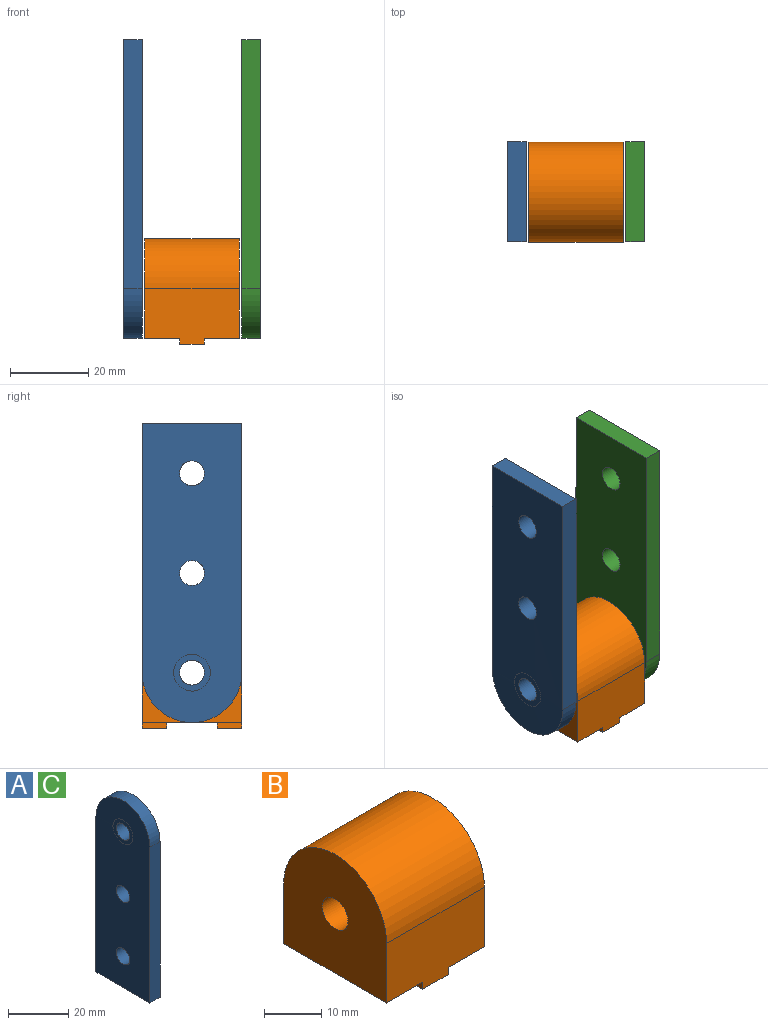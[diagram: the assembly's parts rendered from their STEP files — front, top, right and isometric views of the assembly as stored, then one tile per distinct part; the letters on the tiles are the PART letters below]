
ASSEMBLY  parts=3 mates=3
PART A: 11 faces, bbox 4.8x25.4x76.2 mm
  f0: cylinder r=12.7mm len=25.4mm, axis (-1,0,0), area 190mm2, adj f1,f5,f6,f7
  f1: plane 63.5x4.76mm, normal (0,-1,0), area 302.4mm2, adj f0,f2,f6,f7
  f2: plane 25.4x4.76mm, normal (0,0,-1), area 121mm2, adj f1,f5,f6,f7
  f3: cylinder r=3.17mm len=6.35mm, axis (-1,0,0), area 95mm2, adj f6,f7
  f4: cylinder r=3.17mm len=6.35mm, axis (-1,0,0), area 95mm2, adj f6,f7
  f5: plane 63.5x4.76mm, normal (0,1,0), area 302.4mm2, adj f0,f2,f6,f7
  f6: plane 76.21x25.41mm, normal (1,0,0), area 1733.6mm2, adj f0,f1,f2,f3,f4,f5,f9
  f7: plane 76.21x25.41mm, normal (-1,0,0), area 1733.6mm2, adj f0,f1,f2,f3,f4,f5,f10
  f8: cylinder r=3.17mm len=6.35mm, axis (-1,0,0), area 94.8mm2, adj f9,f10
  f9: plane 9.41x9.41mm, normal (1,0,0), area 37.7mm2, adj f6,f8
  f10: plane 9.41x9.41mm, normal (-1,0,0), area 37.7mm2, adj f7,f8
PART B: 15 faces, bbox 24.1x25.4x26.9 mm
  f0: plane 6.22x1.52mm, normal (-1,0,0), area 9.5mm2, adj f1,f4,f5,f14
  f1: plane 6.22x6.22mm, normal (0,0,-1), area 38.7mm2, adj f0,f2,f4,f14
  f2: plane 6.22x1.52mm, normal (1,0,0), area 9.5mm2, adj f1,f4,f5,f14
  f3: cylinder r=12.7mm len=25.4mm, axis (-1,0,0), area 962.7mm2, adj f4,f7,f8,f9
  f4: plane 24.13x14.22mm, normal (0,-1,0), area 315.9mm2, adj f0,f1,f2,f3,f5,f8,f9
  f5: plane 25.4x24.13mm, normal (0,0,-1), area 535.5mm2, adj f0,f2,f4,f7,f8,f9,f10,f12
  f6: cylinder r=3.17mm len=24.13mm, axis (-1,0,0), area 481.4mm2, adj f8,f9
  f7: plane 24.13x14.22mm, normal (0,1,0), area 315.9mm2, adj f3,f5,f8,f9,f10,f11,f12
  f8: plane 25.4x25.4mm, normal (1,0,0), area 544.3mm2, adj f3,f4,f5,f6,f7
  f9: plane 25.4x25.4mm, normal (-1,0,0), area 544.3mm2, adj f3,f4,f5,f6,f7
  f10: plane 6.22x1.52mm, normal (-1,0,0), area 9.5mm2, adj f5,f7,f11,f13
  f11: plane 6.22x6.22mm, normal (0,0,-1), area 38.7mm2, adj f7,f10,f12,f13
  f12: plane 6.22x1.52mm, normal (1,0,0), area 9.5mm2, adj f5,f7,f11,f13
  f13: plane 6.22x1.52mm, normal (0,-1,0), area 9.5mm2, adj f5,f10,f11,f12
  f14: plane 6.22x1.52mm, normal (0,1,0), area 9.5mm2, adj f0,f1,f2,f5
PART C: same geometry as A
PLACE A rot(axis=(0,-1,0),180deg) t=(-15.08,12.7,76.2)mm
PLACE B at identity fixed
PLACE C rot(axis=(-1,0,0),180deg) t=(15.08,-12.7,76.2)mm
MATE cylindrical C.f3 <-> A.f3  axis (1,0,0) through (17.46,0,63.5)mm
MATE revolute B.f3 <-> C.f0  axis (1,0,0) through (12.07,0,12.7)mm
MATE revolute B.f3 <-> A.f0  axis (1,0,0) through (-12.07,0,12.7)mm
